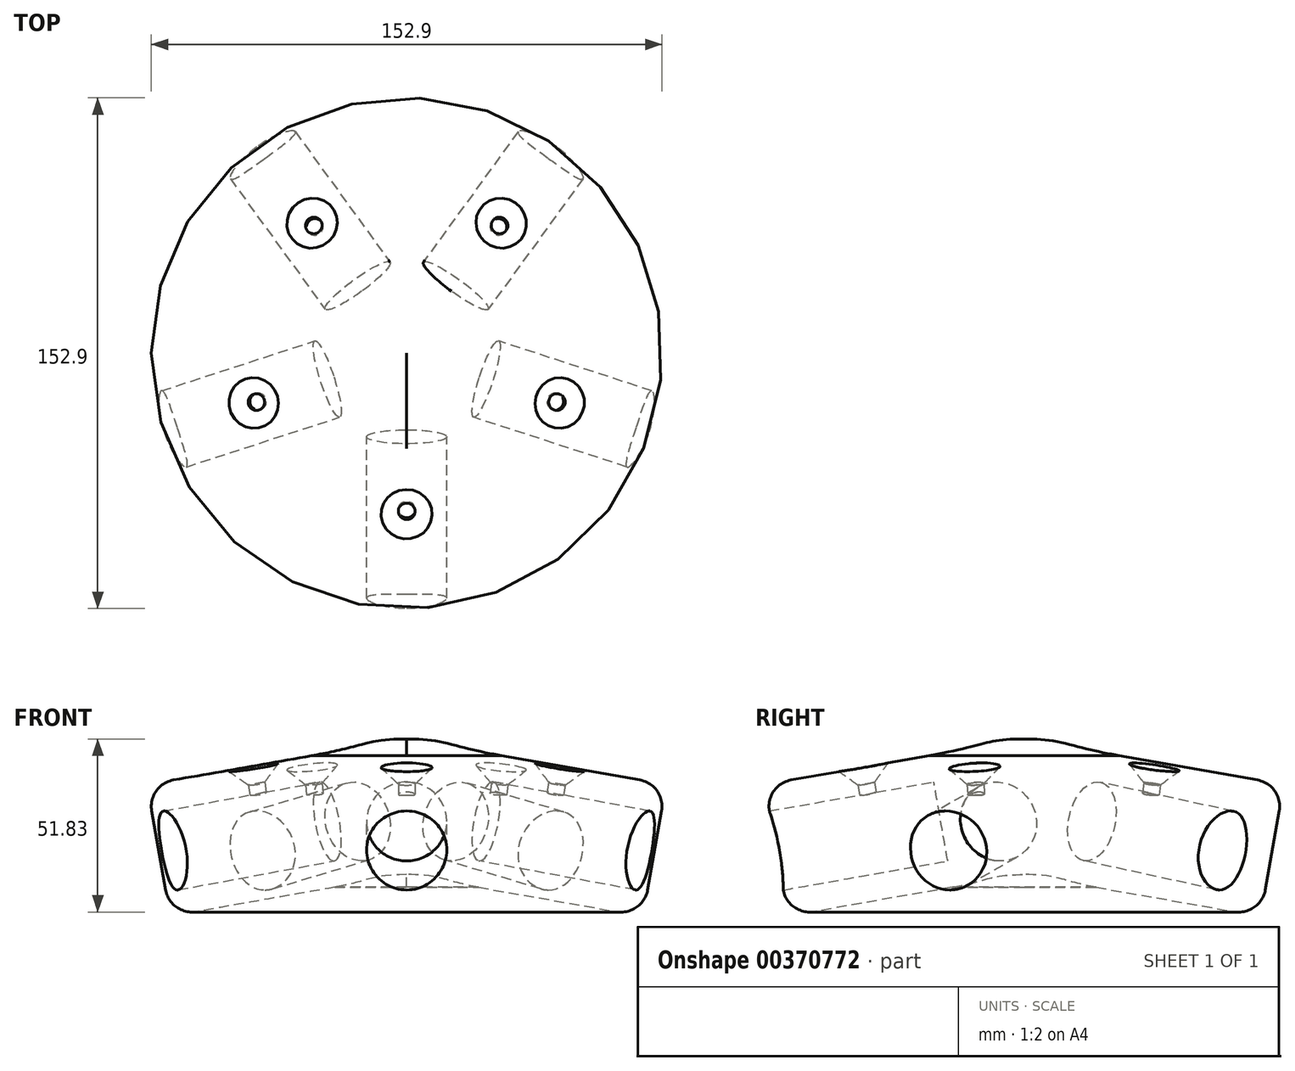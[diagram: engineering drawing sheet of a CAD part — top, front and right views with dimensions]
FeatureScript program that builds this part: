
annotation { "Feature Type Name" : "Feature", "Feature Type Description" : "" }
export const myFeature = defineFeature(function(context is Context, id is Id, definition is map)
    precondition{}
    {
        {
            var Q0;
            Q0=qCreatedBy(makeId("Front.planeOp"),FACE);
            var sketch = newSketch(context, id + "F0", { "sketchPlane" : qUnion([Q0])});
            skCircle(sketch, "E0", {"center": v(0, 0) * mm, "radius": 12 * mm});
            skLineSegment(sketch, "E1", {"start": v(26.12, 0) * mm, "end": v(-31.13, 0) * mm, "construction": true});
            skLineSegment(sketch, "E2", {"start": v(0, 24.39) * mm, "end": v(0, -32.9) * mm, "construction": true});
            skSolve(sketch);
        }
        {
            var Q0;
            Q0=makeQuery(id+"F0.imprint","IMPRINT",FACE,{"disambiguationData":[TD([[makeQuery(id+"F0.imprint","IMPRINT",EDGE,{"derivedFrom":sQuery(id+"F0.wireOp",EDGE,"E0")}),1.0]])]});
            extrude(context, id + "F1", {"entities" : qUnion([Q0]), "depth" : 1220 * mm});
        }
        {
            var Q0;
            Q0=qCreatedBy(makeId("Top.planeOp"),FACE);
            var sketch = newSketch(context, id + "F2", { "sketchPlane" : qUnion([Q0])});
            skLineSegment(sketch, "E3", {"start": v(0, 11.8) * mm, "end": v(0, -46) * mm, "construction": true});
            skCircle(sketch, "E4", {"center": v(0, -20) * mm, "radius": 2.5 * mm});
            skSolve(sketch);
        }
        {
            var Q0;
            Q0 = qSketchRegion(id + "F2", true);
            extrude(context, id + "F3", {"entities" : qUnion([Q0]), "operationType" : NewBodyOperationType.ADD, "depth" : 25 * mm});
        }
        {
            var Q0;
            Q0=makeQuery(id+"F1.opExtrude","SWEPT_BODY",BODY,{"disambiguationData":[OSD([sQuery(id+"F0.wireOp",EDGE,"E0")])]});
            var Q1;
            Q1=sQuery(id+"F0.wireOp",EDGE,"E1");
            transform(context, id + "F4", {"entities" : qUnion([Q0]), "transformType" : TransformType.ROTATION, "transformAxis" : qUnion([Q1]), "angle" : 10 * degree, "oppositeDirection" : true, "makeCopy" : false});
        }
        {
            var Q0;
            Q0=makeQuery(id+"F1.opExtrude","SWEPT_BODY",BODY,{"disambiguationData":[OSD([sQuery(id+"F0.wireOp",EDGE,"E0")])]});
            transform(context, id + "F5", {"entities" : qUnion([Q0]), "transformType" : TransformType.TRANSLATION_3D, "dx" : 0 * mm, "dy" : -25 * mm, "dz" : 0 * mm, "makeCopy" : false});
        }
        {
            var Q0;
            Q0=makeQuery(id+"F1.opExtrude","SWEPT_BODY",BODY,{"disambiguationData":[OSD([sQuery(id+"F0.wireOp",EDGE,"E0")])]});
            var Q1;
            Q1=sQuery(id+"F0.wireOp",EDGE,"E2");
            circularPattern(context, id + "F6", {"entities" : qUnion([Q0]), "axis" : qUnion([Q1]), "angle" : 360 * degree, "instanceCount" : 5, "equalSpace" : true});
        }
        {
            var Q0;
            Q0=qCreatedBy(makeId("Right.planeOp"),FACE);
            var sketch = newSketch(context, id + "F7", { "sketchPlane" : qUnion([Q0])});
            skLineSegment(sketch, "E5.0", {"start": v(-72.16, -20.5) * mm, "end": v(-76.32, 3.14) * mm});
            skLineSegment(sketch, "E6", {"start": v(0, 0) * mm, "end": v(-25, 0) * mm, "construction": true});
            skLineSegment(sketch, "E7", {"start": v(-74.24, -8.68) * mm, "end": v(-25, 0) * mm, "construction": true});
            skLineSegment(sketch, "E8", {"start": v(0, -15.9) * mm, "end": v(0, 24.72) * mm});
            skLineSegment(sketch, "E9", {"start": v(0, 24.72) * mm, "end": v(-69.83, 12.4) * mm, "construction": true});
            skLineSegment(sketch, "E10", {"start": v(-69.83, 12.4) * mm, "end": v(-62.89, -26.99) * mm, "construction": true});
            skLineSegment(sketch, "E11", {"start": v(-62.89, -26.99) * mm, "end": v(0, -15.9) * mm, "construction": true});
            skLineSegment(sketch, "E12", {"start": v(0, 24.72) * mm, "end": v(12.2, 24.72) * mm, "construction": true});
            skLineSegment(sketch, "E13", {"start": v(0, -15.9) * mm, "end": v(12.37, -15.9) * mm, "construction": true});
            skLineSegment(sketch, "E14", {"start": v(-21.53, -19.7) * mm, "end": v(-28.47, 19.7) * mm, "construction": true});
            skLineSegment(sketch, "E15", {"start": v(-69.83, 12.4) * mm, "end": v(-28.47, 19.7) * mm});
            skLineSegment(sketch, "E16", {"start": v(-62.89, -26.99) * mm, "end": v(-21.53, -19.7) * mm});
            skArc(sketch, "E17", {"start": v(-69.83, 12.4) * mm, "mid": v(-75, 9.11) * mm, "end": v(-76.32, 3.14) * mm});
            skArc(sketch, "E18", {"start": v(-72.16, -20.5) * mm, "mid": v(-68.87, -25.66) * mm, "end": v(-62.89, -26.99) * mm});
            skFitSpline(sketch, "E19", {"points": [v(-21.53, -19.7) * mm, v(0, -15.9) * mm], "startDerivative": vector(32.34, 5.7) * mm, "endDerivative": vector(32.41, 0) * mm});
            skFitSpline(sketch, "E20", {"points": [v(-28.47, 19.7) * mm, v(0, 24.72) * mm], "startDerivative": vector(49.5, 8.73) * mm, "endDerivative": vector(36.11, 0) * mm});
            skLineSegment(sketch, "E21", {"start": v(-74.24, -8.68) * mm, "end": v(0, 4.4) * mm, "construction": true});
            skLineSegment(sketch, "E22", {"start": v(-12.18, 29.37) * mm, "end": v(-10.57, -23.73) * mm, "construction": true});
            skPoint(sketch, "E22.startSnap0", {"position": v(-12.18, 0.03) * mm});
            skSolve(sketch);
        }
        {
            var Q0;
            Q0 = qSketchRegion(id + "F7", true);
            var Q1;
            Q1=sQuery(id+"F7.wireOp",EDGE,"E8");
            revolve(context, id + "F8", {"entities" : qUnion([Q0]), "axis" : qUnion([Q1]), "revolveType" : RevolveType.FULL});
        }
        {
            var Q0;
            Q0=makeQuery(id+"F1.opExtrude","SWEPT_BODY",BODY,{"disambiguationData":[OSD([sQuery(id+"F0.wireOp",EDGE,"E0")])]});
            var Q1;
            Q1=makeQuery(id+"F6.opPattern","COPY",BODY,{"derivedFrom":makeQuery(id+"F1.opExtrude","SWEPT_BODY",BODY,{"disambiguationData":[OSD([sQuery(id+"F0.wireOp",EDGE,"E0")])]}),"instanceName":"1"});
            var Q2;
            Q2=makeQuery(id+"F6.opPattern","COPY",BODY,{"derivedFrom":makeQuery(id+"F1.opExtrude","SWEPT_BODY",BODY,{"disambiguationData":[OSD([sQuery(id+"F0.wireOp",EDGE,"E0")])]}),"instanceName":"2"});
            var Q3;
            Q3=makeQuery(id+"F6.opPattern","COPY",BODY,{"derivedFrom":makeQuery(id+"F1.opExtrude","SWEPT_BODY",BODY,{"disambiguationData":[OSD([sQuery(id+"F0.wireOp",EDGE,"E0")])]}),"instanceName":"3"});
            var Q4;
            Q4=makeQuery(id+"F6.opPattern","COPY",BODY,{"derivedFrom":makeQuery(id+"F1.opExtrude","SWEPT_BODY",BODY,{"disambiguationData":[OSD([sQuery(id+"F0.wireOp",EDGE,"E0")])]}),"instanceName":"4"});
            var Q5;
            Q5=makeQuery(id+"F8.opRevolve","SWEPT_BODY",BODY,{"disambiguationData":[OSD([sQuery(id+"F7.wireOp",EDGE,"E5.0"),sQuery(id+"F7.wireOp",EDGE,"E8"),sQuery(id+"F7.wireOp",EDGE,"E15"),sQuery(id+"F7.wireOp",EDGE,"E16"),sQuery(id+"F7.wireOp",EDGE,"E17"),sQuery(id+"F7.wireOp",EDGE,"E18"),sQuery(id+"F7.wireOp",EDGE,"E19"),sQuery(id+"F7.wireOp",EDGE,"E20")])]});
            booleanBodies(context, id + "F9", {"operationType" : BooleanOperationType.SUBTRACTION, "tools" : qUnion([Q0, Q1, Q2, Q3, Q4]), "targets" : qUnion([Q5])});
        }
        {
            var Q0;
            Q0=makeQuery(id+"F9.opBoolean","INTERSECT",EDGE,{"derivedFrom":[makeQuery(id+"F6.opPattern","COPY",FACE,{"derivedFrom":makeQuery(id+"F3.opExtrude","SWEPT_FACE",FACE,{"disambiguationData":[OSD([sQuery(id+"F2.wireOp",EDGE,"E4")])]}),"instanceName":"2"}),makeQuery(id+"F8.opRevolve","SWEPT_FACE",FACE,{"disambiguationData":[OSD([sQuery(id+"F7.wireOp",EDGE,"E15")])]})]});
            var Q1;
            Q1=makeQuery(id+"F9.opBoolean","INTERSECT",EDGE,{"derivedFrom":[makeQuery(id+"F6.opPattern","COPY",FACE,{"derivedFrom":makeQuery(id+"F3.opExtrude","SWEPT_FACE",FACE,{"disambiguationData":[OSD([sQuery(id+"F2.wireOp",EDGE,"E4")])]}),"instanceName":"3"}),makeQuery(id+"F8.opRevolve","SWEPT_FACE",FACE,{"disambiguationData":[OSD([sQuery(id+"F7.wireOp",EDGE,"E15")])]})]});
            var Q2;
            Q2=makeQuery(id+"F9.opBoolean","INTERSECT",EDGE,{"derivedFrom":[makeQuery(id+"F6.opPattern","COPY",FACE,{"derivedFrom":makeQuery(id+"F3.opExtrude","SWEPT_FACE",FACE,{"disambiguationData":[OSD([sQuery(id+"F2.wireOp",EDGE,"E4")])]}),"instanceName":"4"}),makeQuery(id+"F8.opRevolve","SWEPT_FACE",FACE,{"disambiguationData":[OSD([sQuery(id+"F7.wireOp",EDGE,"E15")])]})]});
            var Q3;
            Q3=makeQuery(id+"F9.opBoolean","INTERSECT",EDGE,{"derivedFrom":[makeQuery(id+"F3.opExtrude","SWEPT_FACE",FACE,{"disambiguationData":[OSD([sQuery(id+"F2.wireOp",EDGE,"E4")])]}),makeQuery(id+"F8.opRevolve","SWEPT_FACE",FACE,{"disambiguationData":[OSD([sQuery(id+"F7.wireOp",EDGE,"E15")])]})]});
            var Q4;
            Q4=makeQuery(id+"F9.opBoolean","INTERSECT",EDGE,{"derivedFrom":[makeQuery(id+"F6.opPattern","COPY",FACE,{"derivedFrom":makeQuery(id+"F3.opExtrude","SWEPT_FACE",FACE,{"disambiguationData":[OSD([sQuery(id+"F2.wireOp",EDGE,"E4")])]}),"instanceName":"1"}),makeQuery(id+"F8.opRevolve","SWEPT_FACE",FACE,{"disambiguationData":[OSD([sQuery(id+"F7.wireOp",EDGE,"E15")])]})]});
            chamfer(context, id + "F10", {"entities" : qUnion([Q0, Q1, Q2, Q3, Q4]), "width" : 5 * mm, "tangentPropagation" : true});
        }
    });
